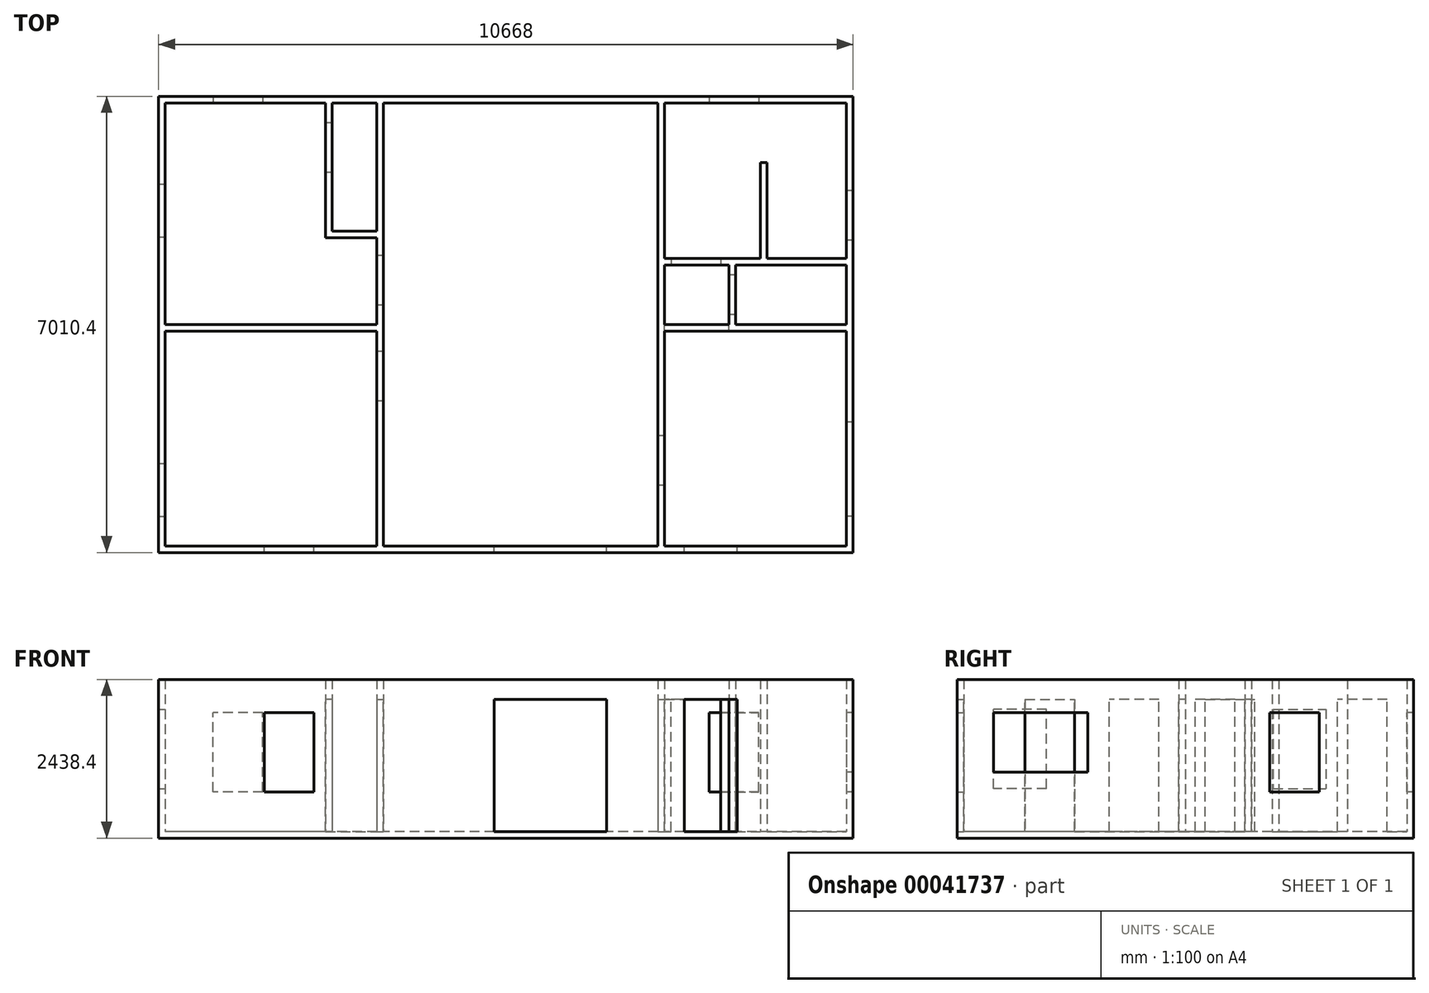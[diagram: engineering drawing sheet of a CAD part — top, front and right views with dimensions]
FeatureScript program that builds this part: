
annotation { "Feature Type Name" : "Feature", "Feature Type Description" : "" }
export const myFeature = defineFeature(function(context is Context, id is Id, definition is map)
    precondition{}
    {
        {
            var Q0;
            Q0=qCreatedBy(makeId("Top.planeOp"),FACE);
            var sketch = newSketch(context, id + "F32", { "sketchPlane" : qUnion([Q0])});
            skLineSegment(sketch, "E0.bottom", {"start": v(10668, 7010.4) * mm, "end": v(0, 7010.4) * mm});
            skLineSegment(sketch, "E0.top", {"start": v(10668, 0) * mm, "end": v(0, 0) * mm});
            skLineSegment(sketch, "E0.left", {"start": v(10668, 7010.4) * mm, "end": v(10668, 0) * mm});
            skLineSegment(sketch, "E0.right", {"start": v(0, 7010.4) * mm, "end": v(0, 0) * mm});
            skSolve(sketch);
        }
        {
            var Q0;
            Q0=qSketchRegion(id+"F32",true);
            extrude(context, id + "F0", {"entities" : qUnion([Q0]), "depth" : 2438.4 * mm});
        }
        {
            var Q0;
            Q0=makeQuery(id+"F0.opExtrude","CAP_FACE",FACE,{"disambiguationData":[OSD([sQuery(id+"F32.wireOp",EDGE,"E0.bottom"),sQuery(id+"F32.wireOp",EDGE,"E0.top"),sQuery(id+"F32.wireOp",EDGE,"E0.left"),sQuery(id+"F32.wireOp",EDGE,"E0.right")])],"isStart":false});
            shell(context, id + "F33", {"entities" : qUnion([Q0]), "thickness" : 101.6 * mm});
        }
        {
            var Q0;
            Q0=makeQuery(id+"F33.opShell","OFFSET_FACE",FACE,{"disambiguationData":[OSD([sQuery(id+"F32.wireOp",EDGE,"E0.bottom"),sQuery(id+"F32.wireOp",EDGE,"E0.top"),sQuery(id+"F32.wireOp",EDGE,"E0.left"),sQuery(id+"F32.wireOp",EDGE,"E0.right")])]});
            var sketch = newSketch(context, id + "F1", { "sketchPlane" : qUnion([Q0])});
            skLineSegment(sketch, "E1", {"start": v(10566.4, 3403.6) * mm, "end": v(7772.4, 3403.6) * mm});
            skLineSegment(sketch, "E2.1", {"start": v(10566.4, 3505.2) * mm, "end": v(8864.6, 3505.2) * mm});
            skLineSegment(sketch, "E3", {"start": v(3454.4, 6908.8) * mm, "end": v(3454.4, 101.6) * mm});
            skLineSegment(sketch, "E4.0", {"start": v(3352.8, 6908.8) * mm, "end": v(3352.8, 3505.2) * mm});
            skLineSegment(sketch, "E5.bottom", {"start": v(2565.4, 3505.2) * mm, "end": v(2667, 3505.2) * mm});
            skLineSegment(sketch, "E5.top", {"start": v(2565.4, 6908.8) * mm, "end": v(2667, 6908.8) * mm});
            skLineSegment(sketch, "E5.left", {"start": v(2565.4, 4834.62) * mm, "end": v(2565.4, 6908.8) * mm});
            skLineSegment(sketch, "E5.right", {"start": v(2667, 4936.22) * mm, "end": v(2667, 6908.8) * mm});
            skLineSegment(sketch, "E6", {"start": v(7670.8, 6908.8) * mm, "end": v(7670.8, 101.6) * mm});
            skLineSegment(sketch, "E7", {"start": v(7772.4, 3505.2) * mm, "end": v(7772.4, 4419.6) * mm});
            skLineSegment(sketch, "E8", {"start": v(7772.4, 3403.6) * mm, "end": v(7772.4, 101.6) * mm});
            skLineSegment(sketch, "E9", {"start": v(3352.8, 3403.6) * mm, "end": v(3352.8, 101.6) * mm});
            skLineSegment(sketch, "E10", {"start": v(2565.4, 4834.62) * mm, "end": v(3352.8, 4834.62) * mm});
            skLineSegment(sketch, "E11", {"start": v(2667, 4936.22) * mm, "end": v(3352.8, 4936.22) * mm});
            skLineSegment(sketch, "E12.trimOffspring", {"start": v(3352.8, 3505.2) * mm, "end": v(101.6, 3505.2) * mm});
            skLineSegment(sketch, "E13.trimOffspring", {"start": v(3352.8, 3403.6) * mm, "end": v(101.6, 3403.6) * mm});
            skLineSegment(sketch, "E14", {"start": v(10566.4, 4419.6) * mm, "end": v(8864.6, 4419.6) * mm});
            skLineSegment(sketch, "E15", {"start": v(8864.6, 4419.6) * mm, "end": v(8864.6, 3505.2) * mm});
            skLineSegment(sketch, "E16", {"start": v(8763, 3505.2) * mm, "end": v(8763, 4419.6) * mm});
            skLineSegment(sketch, "E17", {"start": v(7772.4, 4521.2) * mm, "end": v(9245.6, 4521.2) * mm});
            skLineSegment(sketch, "E18.trimOffspring", {"start": v(8763, 3505.2) * mm, "end": v(7772.4, 3505.2) * mm});
            skLineSegment(sketch, "E19.trimOffspring", {"start": v(8763, 4419.6) * mm, "end": v(7772.4, 4419.6) * mm});
            skLineSegment(sketch, "E20.trimOffspring", {"start": v(7772.4, 4521.2) * mm, "end": v(7772.4, 6908.8) * mm});
            skLineSegment(sketch, "E21", {"start": v(9245.6, 4521.2) * mm, "end": v(9245.6, 5994.4) * mm});
            skLineSegment(sketch, "E22", {"start": v(9347.2, 5994.4) * mm, "end": v(9245.6, 5994.4) * mm});
            skLineSegment(sketch, "E23", {"start": v(9347.2, 5994.4) * mm, "end": v(9347.2, 4521.2) * mm});
            skLineSegment(sketch, "E24.trimOffspring", {"start": v(9347.2, 4521.2) * mm, "end": v(10566.4, 4521.2) * mm});
            skSolve(sketch);
        }
        {
            var Q0;
            {var subQ0=sQuery(id+"F1.wireOp",EDGE,"E3");Q0=makeQuery(id+"F1.imprint","IMPRINT",FACE,{"disambiguationData":[TD([[makeQuery(id+"F1.imprint","IMPRINT",EDGE,{"derivedFrom":subQ0}),-1.0]])]});}
            var Q1;
            {var subQ3=sQuery(id+"F1.wireOp",EDGE,"E1");Q1=makeQuery(id+"F1.imprint","IMPRINT",FACE,{"disambiguationData":[TD([[makeQuery(id+"F1.imprint","IMPRINT",EDGE,{"derivedFrom":subQ3}),-1.0]])]});}
            var Q2;
            Q2=makeQuery(id+"F1.imprint","IMPRINT",FACE,{"disambiguationData":[TD([[makeQuery(id+"F1.imprint","IMPRINT",EDGE,{"derivedFrom":sQuery(id+"F1.wireOp",EDGE,"E5.top")}),1.0]])]});
            var Q3;
            Q3=makeQuery(id+"F0.opExtrude","CAP_FACE",FACE,{"disambiguationData":[OSD([sQuery(id+"F32.wireOp",EDGE,"E0.bottom"),sQuery(id+"F32.wireOp",EDGE,"E0.top"),sQuery(id+"F32.wireOp",EDGE,"E0.left"),sQuery(id+"F32.wireOp",EDGE,"E0.right")])],"isStart":false});
            extrude(context, id + "F2", {"entities" : qUnion([Q0, Q1, Q2]), "operationType" : NewBodyOperationType.ADD, "endBound" : BoundingType.UP_TO_SURFACE, "endBoundEntityFace" : qUnion([Q3]), "depth" : 30.48 * mm, "offsetDistance" : 30.48 * mm});
        }
        {
            var Q0;
            Q0=makeQuery(id+"F33.opShell","OFFSET_FACE",FACE,{"disambiguationData":[OSD([sQuery(id+"F32.wireOp",EDGE,"E0.top")])]});
            var sketch = newSketch(context, id + "F34", { "sketchPlane" : qUnion([Q0])});
            skLineSegment(sketch, "E25.bottom", {"start": v(-8890, 101.6) * mm, "end": v(-8077.2, 101.6) * mm});
            skLineSegment(sketch, "E25.top", {"start": v(-8890, 2133.6) * mm, "end": v(-8077.2, 2133.6) * mm});
            skLineSegment(sketch, "E25.left", {"start": v(-8890, 101.6) * mm, "end": v(-8890, 2133.6) * mm});
            skLineSegment(sketch, "E25.right", {"start": v(-8077.2, 101.6) * mm, "end": v(-8077.2, 2133.6) * mm});
            skSolve(sketch);
        }
        {
            var Q0;
            Q0=qSketchRegion(id+"F34",true);
            extrude(context, id + "F35", {"entities" : qUnion([Q0]), "operationType" : NewBodyOperationType.REMOVE, "endBound" : BoundingType.UP_TO_NEXT, "oppositeDirection" : true, "depth" : 30.48 * mm});
        }
        {
            var Q0;
            {var subQ0=sQuery(id+"F32.wireOp",EDGE,"E0.right");var subQ3=sQuery(id+"F32.wireOp",EDGE,"E0.bottom");Q0=makeQuery(id+"F2.boolean.opBoolean","SPLIT",FACE,{"disambiguationData":[TD([makeQuery(id+"F33.opShell","OFFSET_FACE",FACE,{"disambiguationData":[OSD([subQ3])]})])],"derivedFrom":makeQuery(id+"F33.opShell","OFFSET_FACE",FACE,{"disambiguationData":[OSD([subQ0])]})});}
            var sketch = newSketch(context, id + "F3", { "sketchPlane" : qUnion([Q0])});
            skLineSegment(sketch, "E26.bottom", {"start": v(4851.4, 1981.2) * mm, "end": v(5664.2, 1981.2) * mm});
            skLineSegment(sketch, "E26.top", {"start": v(4851.4, 762) * mm, "end": v(5664.2, 762) * mm});
            skLineSegment(sketch, "E26.left", {"start": v(4851.4, 1981.2) * mm, "end": v(4851.4, 762) * mm});
            skLineSegment(sketch, "E26.right", {"start": v(5664.2, 1981.2) * mm, "end": v(5664.2, 762) * mm});
            skSolve(sketch);
        }
        {
            var Q0;
            Q0=qSketchRegion(id+"F3",true);
            extrude(context, id + "F4", {"entities" : qUnion([Q0]), "operationType" : NewBodyOperationType.REMOVE, "endBound" : BoundingType.UP_TO_NEXT, "oppositeDirection" : true, "depth" : 30.48 * mm});
        }
        {
            var Q0;
            Q0=makeQuery(id+"F33.opShell","OFFSET_FACE",FACE,{"disambiguationData":[OSD([sQuery(id+"F32.wireOp",EDGE,"E0.bottom")])]});
            var sketch = newSketch(context, id + "F5", { "sketchPlane" : qUnion([Q0])});
            skLineSegment(sketch, "E27.bottom", {"start": v(838.2, 1930.4) * mm, "end": v(1600.2, 1930.4) * mm});
            skLineSegment(sketch, "E27.top", {"start": v(838.2, 711.2) * mm, "end": v(1600.2, 711.2) * mm});
            skLineSegment(sketch, "E27.left", {"start": v(838.2, 1930.4) * mm, "end": v(838.2, 711.2) * mm});
            skLineSegment(sketch, "E27.right", {"start": v(1600.2, 1930.4) * mm, "end": v(1600.2, 711.2) * mm});
            skSolve(sketch);
        }
        {
            var Q0;
            Q0=qSketchRegion(id+"F5",true);
            extrude(context, id + "F36", {"entities" : qUnion([Q0]), "operationType" : NewBodyOperationType.REMOVE, "endBound" : BoundingType.UP_TO_NEXT, "oppositeDirection" : true, "depth" : 30.48 * mm});
        }
        {
            var Q0;
            Q0=makeQuery(id+"F2.opExtrude","SWEPT_FACE",FACE,{"disambiguationData":[OSD([sQuery(id+"F1.wireOp",EDGE,"E8")])]});
            var sketch = newSketch(context, id + "F6", { "sketchPlane" : qUnion([Q0])});
            skLineSegment(sketch, "E28.bottom", {"start": v(1041.4, 101.6) * mm, "end": v(1803.4, 101.6) * mm});
            skLineSegment(sketch, "E28.top", {"start": v(1041.4, 2133.6) * mm, "end": v(1803.4, 2133.6) * mm});
            skLineSegment(sketch, "E28.left", {"start": v(1041.4, 101.6) * mm, "end": v(1041.4, 2133.6) * mm});
            skLineSegment(sketch, "E28.right", {"start": v(1803.4, 101.6) * mm, "end": v(1803.4, 2133.6) * mm});
            skSolve(sketch);
        }
        {
            var Q0;
            Q0=qSketchRegion(id+"F6",true);
            extrude(context, id + "F7", {"entities" : qUnion([Q0]), "operationType" : NewBodyOperationType.REMOVE, "endBound" : BoundingType.UP_TO_NEXT, "oppositeDirection" : true, "depth" : 30.48 * mm});
        }
        {
            var Q0;
            {var subQ1=sQuery(id+"F32.wireOp",EDGE,"E0.left");var subQ2=sQuery(id+"F32.wireOp",EDGE,"E0.top");Q0=makeQuery(id+"F2.boolean.opBoolean","SPLIT",FACE,{"disambiguationData":[TD([makeQuery(id+"F33.opShell","OFFSET_FACE",FACE,{"disambiguationData":[OSD([subQ2])]})])],"derivedFrom":makeQuery(id+"F33.opShell","OFFSET_FACE",FACE,{"disambiguationData":[OSD([subQ1])]})});}
            var sketch = newSketch(context, id + "F8", { "sketchPlane" : qUnion([Q0])});
            skLineSegment(sketch, "E29.bottom", {"start": v(-558.8, 1930.4) * mm, "end": v(-2006.6, 1930.4) * mm});
            skLineSegment(sketch, "E29.top", {"start": v(-558.8, 1016) * mm, "end": v(-2006.6, 1016) * mm});
            skLineSegment(sketch, "E29.left", {"start": v(-558.8, 1930.4) * mm, "end": v(-558.8, 1016) * mm});
            skLineSegment(sketch, "E29.right", {"start": v(-2006.6, 1930.4) * mm, "end": v(-2006.6, 1016) * mm});
            skSolve(sketch);
        }
        {
            var Q0;
            Q0=qSketchRegion(id+"F8",true);
            extrude(context, id + "F9", {"entities" : qUnion([Q0]), "operationType" : NewBodyOperationType.REMOVE, "endBound" : BoundingType.UP_TO_NEXT, "oppositeDirection" : true, "depth" : 30.48 * mm});
        }
        {
            var Q0;
            {var subQ1=sQuery(id+"F32.wireOp",EDGE,"E0.left");var subQ3=sQuery(id+"F32.wireOp",EDGE,"E0.bottom");Q0=makeQuery(id+"F2.boolean.opBoolean","SPLIT",FACE,{"disambiguationData":[TD([makeQuery(id+"F33.opShell","OFFSET_FACE",FACE,{"disambiguationData":[OSD([subQ1])]})])],"derivedFrom":makeQuery(id+"F33.opShell","OFFSET_FACE",FACE,{"disambiguationData":[OSD([subQ3])]})});}
            var sketch = newSketch(context, id + "F10", { "sketchPlane" : qUnion([Q0])});
            skLineSegment(sketch, "E30.bottom", {"start": v(8458.2, 711.2) * mm, "end": v(9220.2, 711.2) * mm});
            skLineSegment(sketch, "E30.top", {"start": v(8458.2, 1930.4) * mm, "end": v(9220.2, 1930.4) * mm});
            skLineSegment(sketch, "E30.left", {"start": v(8458.2, 711.2) * mm, "end": v(8458.2, 1930.4) * mm});
            skLineSegment(sketch, "E30.right", {"start": v(9220.2, 711.2) * mm, "end": v(9220.2, 1930.4) * mm});
            skSolve(sketch);
        }
        {
            var Q0;
            Q0=qSketchRegion(id+"F10",true);
            extrude(context, id + "F11", {"entities" : qUnion([Q0]), "operationType" : NewBodyOperationType.REMOVE, "endBound" : BoundingType.UP_TO_NEXT, "oppositeDirection" : true, "depth" : 30.48 * mm});
        }
        {
            var Q0;
            {var subQ1=sQuery(id+"F32.wireOp",EDGE,"E0.left");var subQ3=sQuery(id+"F32.wireOp",EDGE,"E0.bottom");Q0=makeQuery(id+"F2.boolean.opBoolean","SPLIT",FACE,{"disambiguationData":[TD([makeQuery(id+"F33.opShell","OFFSET_FACE",FACE,{"disambiguationData":[OSD([subQ3])]})])],"derivedFrom":makeQuery(id+"F33.opShell","OFFSET_FACE",FACE,{"disambiguationData":[OSD([subQ1])]})});}
            var sketch = newSketch(context, id + "F12", { "sketchPlane" : qUnion([Q0])});
            skLineSegment(sketch, "E31.bottom", {"start": v(-5562.6, 1930.4) * mm, "end": v(-4800.6, 1930.4) * mm});
            skLineSegment(sketch, "E31.top", {"start": v(-5562.6, 711.2) * mm, "end": v(-4800.6, 711.2) * mm});
            skLineSegment(sketch, "E31.left", {"start": v(-5562.6, 1930.4) * mm, "end": v(-5562.6, 711.2) * mm});
            skLineSegment(sketch, "E31.right", {"start": v(-4800.6, 1930.4) * mm, "end": v(-4800.6, 711.2) * mm});
            skSolve(sketch);
        }
        {
            var Q0;
            Q0=qSketchRegion(id+"F12",true);
            extrude(context, id + "F13", {"entities" : qUnion([Q0]), "operationType" : NewBodyOperationType.REMOVE, "endBound" : BoundingType.UP_TO_NEXT, "oppositeDirection" : true, "depth" : 30.48 * mm});
        }
        {
            var Q0;
            {var subQ0=sQuery(id+"F32.wireOp",EDGE,"E0.right");var subQ2=sQuery(id+"F32.wireOp",EDGE,"E0.top");Q0=makeQuery(id+"F2.boolean.opBoolean","SPLIT",FACE,{"disambiguationData":[TD([makeQuery(id+"F33.opShell","OFFSET_FACE",FACE,{"disambiguationData":[OSD([subQ0])]})])],"derivedFrom":makeQuery(id+"F33.opShell","OFFSET_FACE",FACE,{"disambiguationData":[OSD([subQ2])]})});}
            var sketch = newSketch(context, id + "F14", { "sketchPlane" : qUnion([Q0])});
            skLineSegment(sketch, "E32.bottom", {"start": v(-1625.6, 1930.4) * mm, "end": v(-2387.6, 1930.4) * mm});
            skLineSegment(sketch, "E32.top", {"start": v(-1625.6, 711.2) * mm, "end": v(-2387.6, 711.2) * mm});
            skLineSegment(sketch, "E32.left", {"start": v(-1625.6, 1930.4) * mm, "end": v(-1625.6, 711.2) * mm});
            skLineSegment(sketch, "E32.right", {"start": v(-2387.6, 1930.4) * mm, "end": v(-2387.6, 711.2) * mm});
            skSolve(sketch);
        }
        {
            var Q0;
            Q0=qSketchRegion(id+"F14",true);
            extrude(context, id + "F15", {"entities" : qUnion([Q0]), "operationType" : NewBodyOperationType.REMOVE, "endBound" : BoundingType.UP_TO_NEXT, "oppositeDirection" : true, "depth" : 30.48 * mm});
        }
        {
            var Q0;
            {var subQ0=sQuery(id+"F32.wireOp",EDGE,"E0.right");var subQ2=sQuery(id+"F32.wireOp",EDGE,"E0.top");Q0=makeQuery(id+"F2.boolean.opBoolean","SPLIT",FACE,{"disambiguationData":[TD([makeQuery(id+"F33.opShell","OFFSET_FACE",FACE,{"disambiguationData":[OSD([subQ0])]})])],"derivedFrom":makeQuery(id+"F33.opShell","OFFSET_FACE",FACE,{"disambiguationData":[OSD([subQ2])]})});}
            var sketch = newSketch(context, id + "F16", { "sketchPlane" : qUnion([Q0])});
            skLineSegment(sketch, "E33.bottom", {"start": v(-5156.2, 101.6) * mm, "end": v(-6883.4, 101.6) * mm});
            skLineSegment(sketch, "E33.top", {"start": v(-5156.2, 2133.6) * mm, "end": v(-6883.4, 2133.6) * mm});
            skLineSegment(sketch, "E33.left", {"start": v(-5156.2, 101.6) * mm, "end": v(-5156.2, 2133.6) * mm});
            skLineSegment(sketch, "E33.right", {"start": v(-6883.4, 101.6) * mm, "end": v(-6883.4, 2133.6) * mm});
            skSolve(sketch);
        }
        {
            var Q0;
            Q0=qSketchRegion(id+"F16",true);
            extrude(context, id + "F17", {"entities" : qUnion([Q0]), "operationType" : NewBodyOperationType.REMOVE, "endBound" : BoundingType.UP_TO_NEXT, "oppositeDirection" : true, "depth" : 30.48 * mm});
        }
        {
            var Q0;
            Q0=makeQuery(id+"F2.opExtrude","SWEPT_FACE",FACE,{"disambiguationData":[OSD([sQuery(id+"F1.wireOp",EDGE,"E5.left")])]});
            var sketch = newSketch(context, id + "F18", { "sketchPlane" : qUnion([Q0])});
            skLineSegment(sketch, "E34.bottom", {"start": v(-6604, 101.6) * mm, "end": v(-5842, 101.6) * mm});
            skLineSegment(sketch, "E34.top", {"start": v(-6604, 2133.6) * mm, "end": v(-5842, 2133.6) * mm});
            skLineSegment(sketch, "E34.left", {"start": v(-6604, 101.6) * mm, "end": v(-6604, 2133.6) * mm});
            skLineSegment(sketch, "E34.right", {"start": v(-5842, 101.6) * mm, "end": v(-5842, 2133.6) * mm});
            skSolve(sketch);
        }
        {
            var Q0;
            Q0=qSketchRegion(id+"F18",true);
            extrude(context, id + "F19", {"entities" : qUnion([Q0]), "operationType" : NewBodyOperationType.REMOVE, "endBound" : BoundingType.UP_TO_NEXT, "oppositeDirection" : true, "depth" : 30.48 * mm});
        }
        {
            var Q0;
            {var subQ2=sQuery(id+"F32.wireOp",EDGE,"E0.right");var subQ4=sQuery(id+"F32.wireOp",EDGE,"E0.top");Q0=makeQuery(id+"F2.boolean.opBoolean","SPLIT",FACE,{"disambiguationData":[TD([makeQuery(id+"F33.opShell","OFFSET_FACE",FACE,{"disambiguationData":[OSD([subQ4])]})])],"derivedFrom":makeQuery(id+"F33.opShell","OFFSET_FACE",FACE,{"disambiguationData":[OSD([subQ2])]})});}
            var sketch = newSketch(context, id + "F20", { "sketchPlane" : qUnion([Q0])});
            skLineSegment(sketch, "E35.bottom", {"start": v(558.8, 1981.3) * mm, "end": v(1371.6, 1981.3) * mm});
            skLineSegment(sketch, "E35.top", {"start": v(558.8, 762.1) * mm, "end": v(1371.6, 762.1) * mm});
            skLineSegment(sketch, "E35.left", {"start": v(558.8, 1981.3) * mm, "end": v(558.8, 762.1) * mm});
            skLineSegment(sketch, "E35.right", {"start": v(1371.6, 1981.3) * mm, "end": v(1371.6, 762.1) * mm});
            skSolve(sketch);
        }
        {
            var Q0;
            Q0 = qSketchRegion(id + "F20", true);
            extrude(context, id + "F21", {"entities" : qUnion([Q0]), "operationType" : NewBodyOperationType.REMOVE, "endBound" : BoundingType.UP_TO_NEXT, "oppositeDirection" : true, "depth" : 30.48 * mm, "offsetDistance" : 30.48 * mm});
        }
        {
            var Q0;
            Q0=makeQuery(id+"F2.opExtrude","SWEPT_FACE",FACE,{"disambiguationData":[OSD([sQuery(id+"F1.wireOp",EDGE,"E3")])]});
            var sketch = newSketch(context, id + "F22", { "sketchPlane" : qUnion([Q0])});
            skLineSegment(sketch, "E36.bottom", {"start": v(3098.8, 101.6) * mm, "end": v(2336.8, 101.6) * mm});
            skLineSegment(sketch, "E36.top", {"start": v(3098.8, 2133.6) * mm, "end": v(2336.8, 2133.6) * mm});
            skLineSegment(sketch, "E36.left", {"start": v(3098.8, 101.6) * mm, "end": v(3098.8, 2133.6) * mm});
            skLineSegment(sketch, "E36.right", {"start": v(2336.8, 101.6) * mm, "end": v(2336.8, 2133.6) * mm});
            skSolve(sketch);
        }
        {
            var Q0;
            Q0 = qSketchRegion(id + "F22", true);
            extrude(context, id + "F23", {"entities" : qUnion([Q0]), "operationType" : NewBodyOperationType.REMOVE, "endBound" : BoundingType.UP_TO_NEXT, "oppositeDirection" : true, "depth" : 30.48 * mm, "offsetDistance" : 30.48 * mm});
        }
        {
            var Q0;
            Q0=makeQuery(id+"F2.opExtrude","SWEPT_FACE",FACE,{"disambiguationData":[OSD([sQuery(id+"F1.wireOp",EDGE,"E3")])]});
            var sketch = newSketch(context, id + "F24", { "sketchPlane" : qUnion([Q0])});
            skLineSegment(sketch, "E37.bottom", {"start": v(3810, 101.6) * mm, "end": v(4572, 101.6) * mm});
            skLineSegment(sketch, "E37.top", {"start": v(3810, 2133.6) * mm, "end": v(4572, 2133.6) * mm});
            skLineSegment(sketch, "E37.left", {"start": v(3810, 101.6) * mm, "end": v(3810, 2133.6) * mm});
            skLineSegment(sketch, "E37.right", {"start": v(4572, 101.6) * mm, "end": v(4572, 2133.6) * mm});
            skSolve(sketch);
        }
        {
            var Q0;
            Q0 = qSketchRegion(id + "F24", true);
            extrude(context, id + "F25", {"entities" : qUnion([Q0]), "operationType" : NewBodyOperationType.REMOVE, "endBound" : BoundingType.UP_TO_NEXT, "oppositeDirection" : true, "depth" : 30.48 * mm, "offsetDistance" : 30.48 * mm});
        }
        {
            var Q0;
            Q0=makeQuery(id+"F2.opExtrude","SWEPT_FACE",FACE,{"disambiguationData":[OSD([sQuery(id+"F1.wireOp",EDGE,"E16")])]});
            var sketch = newSketch(context, id + "F26", { "sketchPlane" : qUnion([Q0])});
            skLineSegment(sketch, "E38.bottom", {"start": v(-4267.2, 101.6) * mm, "end": v(-3657.6, 101.6) * mm});
            skLineSegment(sketch, "E38.top", {"start": v(-4267.2, 2133.6) * mm, "end": v(-3657.6, 2133.6) * mm});
            skLineSegment(sketch, "E38.left", {"start": v(-4267.2, 101.6) * mm, "end": v(-4267.2, 2133.6) * mm});
            skLineSegment(sketch, "E38.right", {"start": v(-3657.6, 101.6) * mm, "end": v(-3657.6, 2133.6) * mm});
            skSolve(sketch);
        }
        {
            var Q0;
            Q0 = qSketchRegion(id + "F26", true);
            extrude(context, id + "F27", {"entities" : qUnion([Q0]), "operationType" : NewBodyOperationType.REMOVE, "endBound" : BoundingType.UP_TO_NEXT, "oppositeDirection" : true, "depth" : 30.48 * mm, "offsetDistance" : 30.48 * mm});
        }
        {
            var Q0;
            Q0=makeQuery(id+"F2.opExtrude","SWEPT_FACE",FACE,{"disambiguationData":[OSD([sQuery(id+"F1.wireOp",EDGE,"E1")])]});
            var sketch = newSketch(context, id + "F28", { "sketchPlane" : qUnion([Q0])});
            skLineSegment(sketch, "E39.bottom", {"start": v(7772.4, 101.6) * mm, "end": v(8763, 101.6) * mm});
            skLineSegment(sketch, "E39.top", {"start": v(7772.4, 2133.6) * mm, "end": v(8763, 2133.6) * mm});
            skLineSegment(sketch, "E39.left", {"start": v(7772.4, 101.6) * mm, "end": v(7772.4, 2133.6) * mm});
            skLineSegment(sketch, "E39.right", {"start": v(8763, 101.6) * mm, "end": v(8763, 2133.6) * mm});
            skSolve(sketch);
        }
        {
            var Q0;
            Q0 = qSketchRegion(id + "F28", true);
            extrude(context, id + "F29", {"entities" : qUnion([Q0]), "operationType" : NewBodyOperationType.REMOVE, "endBound" : BoundingType.UP_TO_NEXT, "oppositeDirection" : true, "depth" : 30.48 * mm, "offsetDistance" : 30.48 * mm});
        }
        {
            var Q0;
            Q0=makeQuery(id+"F2.opExtrude","SWEPT_FACE",FACE,{"disambiguationData":[OSD([sQuery(id+"F1.wireOp",EDGE,"E19.trimOffspring")])]});
            var sketch = newSketch(context, id + "F30", { "sketchPlane" : qUnion([Q0])});
            skLineSegment(sketch, "E40.bottom", {"start": v(8636, 101.6) * mm, "end": v(7874, 101.6) * mm});
            skLineSegment(sketch, "E40.top", {"start": v(8636, 2133.6) * mm, "end": v(7874, 2133.6) * mm});
            skLineSegment(sketch, "E40.left", {"start": v(8636, 101.6) * mm, "end": v(8636, 2133.6) * mm});
            skLineSegment(sketch, "E40.right", {"start": v(7874, 101.6) * mm, "end": v(7874, 2133.6) * mm});
            skSolve(sketch);
        }
        {
            var Q0;
            Q0 = qSketchRegion(id + "F30", true);
            extrude(context, id + "F31", {"entities" : qUnion([Q0]), "operationType" : NewBodyOperationType.REMOVE, "endBound" : BoundingType.UP_TO_NEXT, "oppositeDirection" : true, "depth" : 30.48 * mm, "offsetDistance" : 30.48 * mm});
        }
    });
